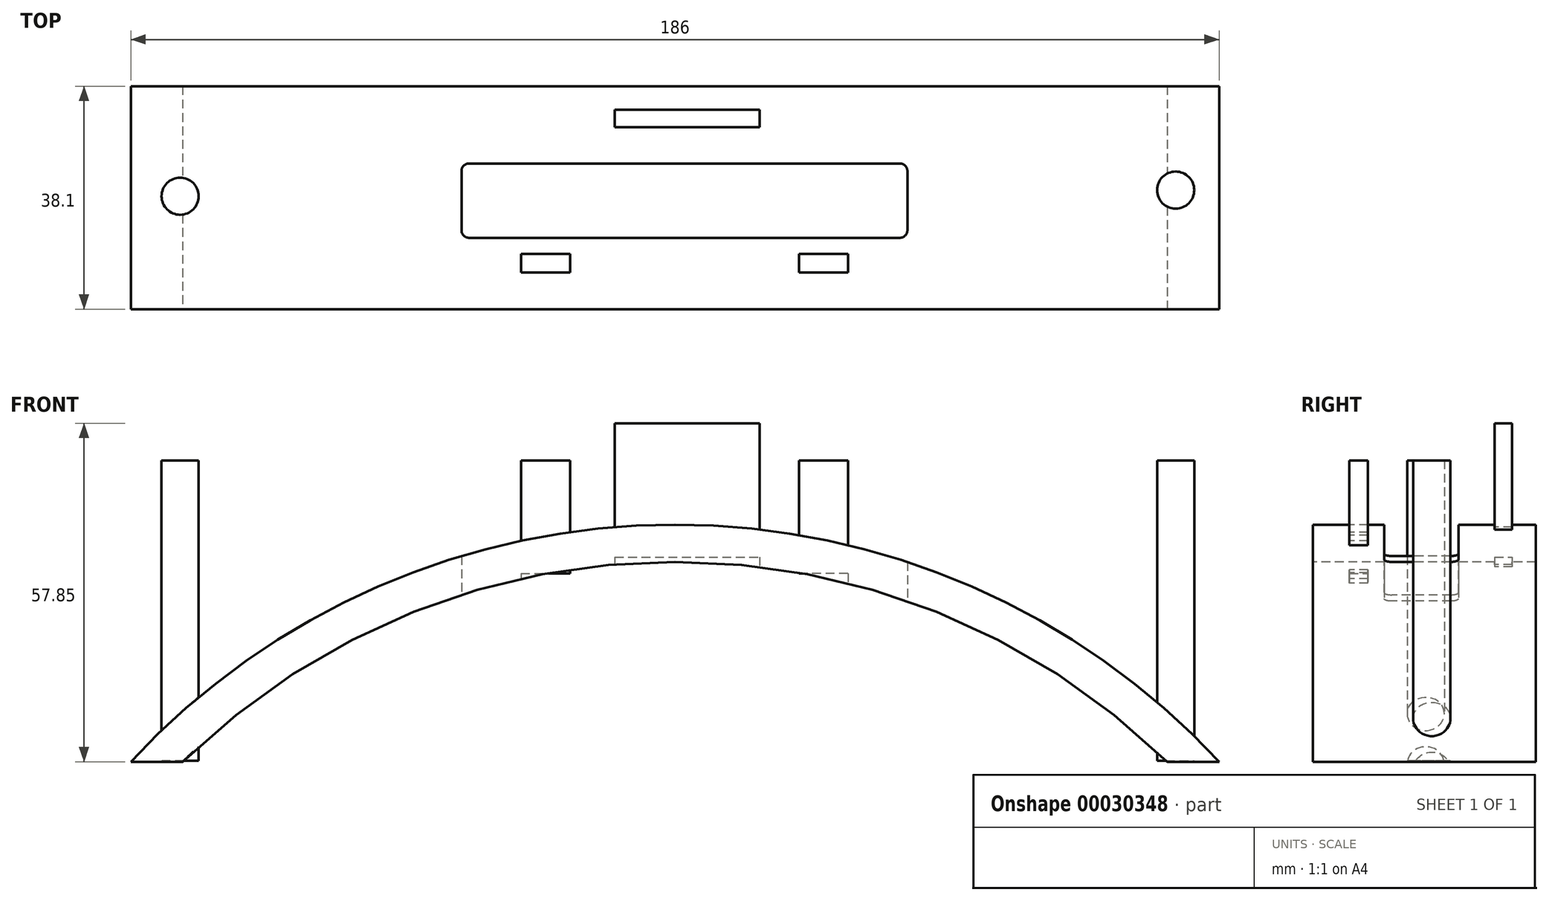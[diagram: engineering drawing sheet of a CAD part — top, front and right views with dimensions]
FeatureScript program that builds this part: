
annotation { "Feature Type Name" : "Feature", "Feature Type Description" : "" }
export const myFeature = defineFeature(function(context is Context, id is Id, definition is map)
    precondition{}
    {
        {
            var Q0;
            Q0=qCreatedBy(makeId("Front.planeOp"),FACE);
            var sketch = newSketch(context, id + "F0", { "sketchPlane" : qUnion([Q0])});
            skArc(sketch, "E0", {"start": v(166.64, 0) * mm, "mid": v(67.07, 52.51) * mm, "end": v(-32.5, 0) * mm});
            skArc(sketch, "E1.0", {"start": v(171.88, 3.59) * mm, "mid": v(67.07, 58.86) * mm, "end": v(-37.74, 3.59) * mm});
            skLineSegment(sketch, "E2", {"start": v(166.64, 0) * mm, "end": v(171.88, 3.59) * mm});
            skLineSegment(sketch, "E3", {"start": v(-32.5, 0) * mm, "end": v(-37.74, 3.59) * mm});
            skSolve(sketch);
        }
        {
            var Q0;
            Q0=makeQuery(id+"F0.imprint","IMPRINT",FACE,{"disambiguationData":[TD([[makeQuery(id+"F0.imprint","IMPRINT",EDGE,{"derivedFrom":sQuery(id+"F0.wireOp",EDGE,"E0")}),-1.0]])]});
            extrude(context, id + "F1", {"entities" : qUnion([Q0]), "oppositeDirection" : true, "depth" : 38.1 * mm});
        }
        {
            var Q0;
            Q0=qCreatedBy(makeId("Top.planeOp"),FACE);
            var sketch = newSketch(context, id + "F2", { "sketchPlane" : qUnion([Q0])});
            skLineSegment(sketch, "E4.bottom", {"start": v(31.85, 24.88) * mm, "end": v(105.5, 24.88) * mm});
            skLineSegment(sketch, "E4.top", {"start": v(31.85, 12.18) * mm, "end": v(105.5, 12.18) * mm});
            skLineSegment(sketch, "E4.left", {"start": v(30.58, 23.61) * mm, "end": v(30.58, 13.45) * mm});
            skLineSegment(sketch, "E4.right", {"start": v(106.78, 23.61) * mm, "end": v(106.78, 13.45) * mm});
            skPoint(sketch, "E5.visualSharp", {"position": v(106.78, 24.88) * mm});
            skArc(sketch, "E5.filletArc", {"start": v(106.78, 23.61) * mm, "mid": v(106.4, 24.5) * mm, "end": v(105.5, 24.88) * mm});
            skPoint(sketch, "E6.visualSharp", {"position": v(30.58, 24.88) * mm});
            skArc(sketch, "E6.filletArc", {"start": v(31.85, 24.88) * mm, "mid": v(30.95, 24.5) * mm, "end": v(30.58, 23.61) * mm});
            skPoint(sketch, "E7.visualSharp", {"position": v(106.78, 12.18) * mm});
            skArc(sketch, "E7.filletArc", {"start": v(105.5, 12.18) * mm, "mid": v(106.4, 12.55) * mm, "end": v(106.78, 13.45) * mm});
            skPoint(sketch, "E8.visualSharp", {"position": v(30.58, 12.18) * mm});
            skArc(sketch, "E8.filletArc", {"start": v(30.58, 13.45) * mm, "mid": v(30.95, 12.55) * mm, "end": v(31.85, 12.18) * mm});
            skSolve(sketch);
        }
        {
            var Q0;
            Q0=makeQuery(id+"F2.imprint","IMPRINT",FACE,{"disambiguationData":[TD([[makeQuery(id+"F2.imprint","IMPRINT",EDGE,{"derivedFrom":sQuery(id+"F2.wireOp",EDGE,"E4.bottom")}),-1.0]])]});
            extrude(context, id + "F3", {"entities" : qUnion([Q0]), "operationType" : NewBodyOperationType.REMOVE, "depth" : 63.5 * mm});
        }
        {
            var Q0;
            Q0=qCreatedBy(makeId("Top.planeOp"),FACE);
            var sketch = newSketch(context, id + "F4", { "sketchPlane" : qUnion([Q0])});
            skCircle(sketch, "E9", {"center": v(-17.5, 19.3) * mm, "radius": 3.17 * mm});
            skCircle(sketch, "E10", {"center": v(152.63, 20.33) * mm, "radius": 3.18 * mm});
            skSolve(sketch);
        }
        {
            var Q0;
            Q0=qCreatedBy(makeId("Top.planeOp"),FACE);
            var sketch = newSketch(context, id + "F5", { "sketchPlane" : qUnion([Q0])});
            skLineSegment(sketch, "E11.bottom", {"start": v(56.77, 31.06) * mm, "end": v(81.53, 31.06) * mm});
            skLineSegment(sketch, "E11.top", {"start": v(56.77, 34.06) * mm, "end": v(81.53, 34.06) * mm});
            skLineSegment(sketch, "E11.left", {"start": v(56.77, 31.06) * mm, "end": v(56.77, 34.06) * mm});
            skLineSegment(sketch, "E11.right", {"start": v(81.53, 31.06) * mm, "end": v(81.53, 34.06) * mm});
            skSolve(sketch);
        }
        {
            var Q0;
            Q0=makeQuery(id+"F4.imprint","IMPRINT",FACE,{"disambiguationData":[TD([[makeQuery(id+"F4.imprint","IMPRINT",EDGE,{"derivedFrom":sQuery(id+"F4.wireOp",EDGE,"E9")}),1.0]])]});
            var Q1;
            Q1=makeQuery(id+"F4.imprint","IMPRINT",FACE,{"disambiguationData":[TD([[makeQuery(id+"F4.imprint","IMPRINT",EDGE,{"derivedFrom":sQuery(id+"F4.wireOp",EDGE,"E10")}),1.0]])]});
            var Q2;
            Q2=sQuery(id+"F4.wireOp",EDGE,"E9");
            var Q3;
            Q3=sQuery(id+"F4.wireOp",EDGE,"E10");
            extrude(context, id + "F6", {"entities" : qUnion([Q0, Q1]), "operationType" : NewBodyOperationType.ADD, "surfaceEntities" : qUnion([Q2, Q3]), "depth" : 69.85 * mm});
        }
        {
            var Q0;
            Q0=makeQuery(id+"F6.opExtrude","CAP_FACE",FACE,{"disambiguationData":[OSD([sQuery(id+"F4.wireOp",EDGE,"E10")])],"isStart":true});
            var Q1;
            Q1=makeQuery(id+"F6.opExtrude","CAP_FACE",FACE,{"disambiguationData":[OSD([sQuery(id+"F4.wireOp",EDGE,"E9")])],"isStart":true});
            extrude(context, id + "F7", {"entities" : qUnion([Q0, Q1]), "operationType" : NewBodyOperationType.REMOVE, "oppositeDirection" : true, "depth" : 18.54 * mm});
        }
        {
            var Q0;
            Q0=makeQuery(id+"F5.imprint","IMPRINT",FACE,{"disambiguationData":[TD([[makeQuery(id+"F5.imprint","IMPRINT",EDGE,{"derivedFrom":sQuery(id+"F5.wireOp",EDGE,"E11.bottom")}),1.0]])]});
            extrude(context, id + "F8", {"entities" : qUnion([Q0]), "operationType" : NewBodyOperationType.ADD, "depth" : 76.2 * mm});
        }
        {
            var Q0;
            Q0=makeQuery(id+"F8.opExtrude","CAP_FACE",FACE,{"disambiguationData":[OSD([sQuery(id+"F5.wireOp",EDGE,"E11.bottom"),sQuery(id+"F5.wireOp",EDGE,"E11.top"),sQuery(id+"F5.wireOp",EDGE,"E11.left"),sQuery(id+"F5.wireOp",EDGE,"E11.right")])],"isStart":true});
            extrude(context, id + "F9", {"entities" : qUnion([Q0]), "operationType" : NewBodyOperationType.REMOVE, "oppositeDirection" : true, "depth" : 53.34 * mm});
        }
        {
            var Q0;
            Q0=qCreatedBy(makeId("Front.planeOp"),FACE);
            var sketch = newSketch(context, id + "F10", { "sketchPlane" : qUnion([Q0])});
            skLineSegment(sketch, "E12.bottom", {"start": v(-44.44, 18.35) * mm, "end": v(177.72, 18.35) * mm});
            skLineSegment(sketch, "E12.top", {"start": v(-44.44, -4.03) * mm, "end": v(177.72, -4.03) * mm});
            skLineSegment(sketch, "E12.left", {"start": v(-44.44, 18.35) * mm, "end": v(-44.44, -4.03) * mm});
            skLineSegment(sketch, "E12.right", {"start": v(177.72, 18.35) * mm, "end": v(177.72, -4.03) * mm});
            skSolve(sketch);
        }
        {
            var Q0;
            Q0=makeQuery(id+"F10.imprint","IMPRINT",FACE,{"disambiguationData":[TD([[makeQuery(id+"F10.imprint","IMPRINT",EDGE,{"derivedFrom":sQuery(id+"F10.wireOp",EDGE,"E12.bottom")}),-1.0]])]});
            extrude(context, id + "F11", {"entities" : qUnion([Q0]), "operationType" : NewBodyOperationType.REMOVE, "oppositeDirection" : true, "depth" : 50.8 * mm});
        }
        {
            var Q0;
            Q0=qCreatedBy(makeId("Top.planeOp"),FACE);
            var sketch = newSketch(context, id + "F12", { "sketchPlane" : qUnion([Q0])});
            skLineSegment(sketch, "E13.bottom", {"start": v(40.74, 6.25) * mm, "end": v(49.12, 6.25) * mm});
            skLineSegment(sketch, "E13.top", {"start": v(40.74, 9.43) * mm, "end": v(49.12, 9.43) * mm});
            skLineSegment(sketch, "E13.left", {"start": v(40.74, 6.25) * mm, "end": v(40.74, 9.43) * mm});
            skLineSegment(sketch, "E13.right", {"start": v(49.12, 6.25) * mm, "end": v(49.12, 9.43) * mm});
            skLineSegment(sketch, "E14.bottom", {"start": v(96.62, 6.25) * mm, "end": v(88.24, 6.25) * mm});
            skLineSegment(sketch, "E14.top", {"start": v(96.62, 9.43) * mm, "end": v(88.24, 9.43) * mm});
            skLineSegment(sketch, "E14.left", {"start": v(96.62, 6.25) * mm, "end": v(96.62, 9.43) * mm});
            skLineSegment(sketch, "E14.right", {"start": v(88.24, 6.25) * mm, "end": v(88.24, 9.43) * mm});
            skSolve(sketch);
        }
        {
            var Q0;
            Q0 = qSketchRegion(id + "F12", true);
            extrude(context, id + "F13", {"entities" : qUnion([Q0]), "operationType" : NewBodyOperationType.ADD, "depth" : 69.85 * mm});
        }
        {
            var Q0;
            Q0 = qSketchRegion(id + "F12", true);
            extrude(context, id + "F14", {"entities" : qUnion([Q0]), "operationType" : NewBodyOperationType.REMOVE, "depth" : 50.55 * mm});
        }
    });
